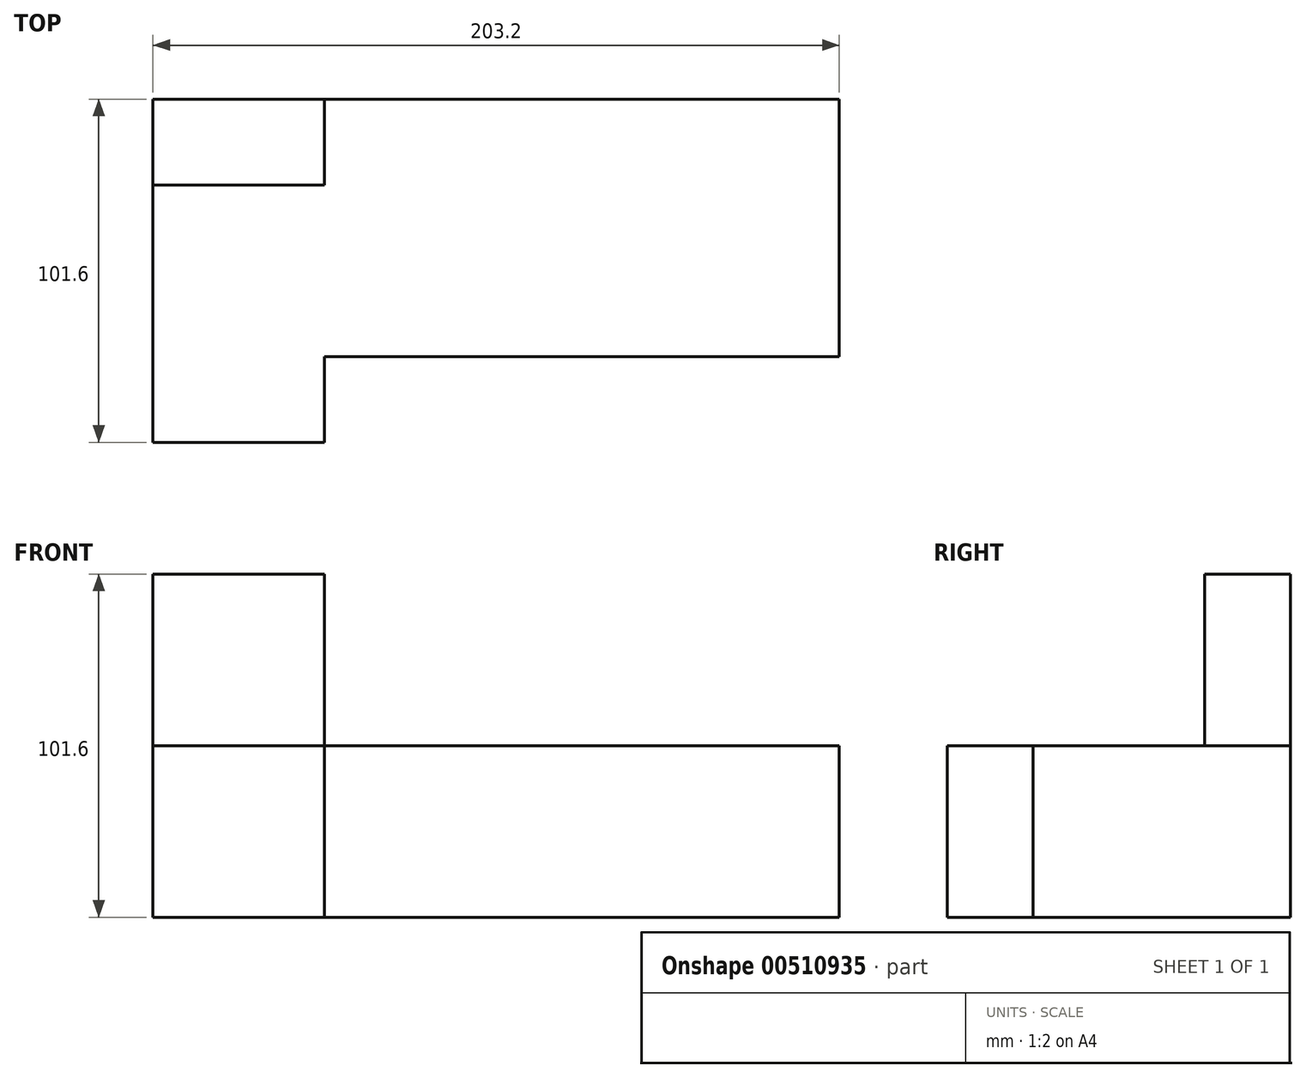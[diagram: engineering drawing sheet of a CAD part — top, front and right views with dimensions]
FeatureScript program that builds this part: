
annotation { "Feature Type Name" : "Feature", "Feature Type Description" : "" }
export const myFeature = defineFeature(function(context is Context, id is Id, definition is map)
    precondition{}
    {
        {
            var Q0;
            Q0=qCreatedBy(makeId("Front.planeOp"),FACE);
            var sketch = newSketch(context, id + "F0", { "sketchPlane" : qUnion([Q0])});
            skLineSegment(sketch, "E0.bottom", {"start": v(-100.78, 50.8) * mm, "end": v(102.42, 50.8) * mm});
            skLineSegment(sketch, "E0.top", {"start": v(-100.78, 0) * mm, "end": v(102.42, 0) * mm});
            skLineSegment(sketch, "E0.left", {"start": v(-100.78, 50.8) * mm, "end": v(-100.78, 0) * mm});
            skLineSegment(sketch, "E0.right", {"start": v(102.42, 50.8) * mm, "end": v(102.42, 0) * mm});
            skSolve(sketch);
        }
        {
            var Q0;
            Q0=makeQuery(id+"F0.imprint","IMPRINT",FACE,{"disambiguationData":[TD([[makeQuery(id+"F0.imprint","IMPRINT",EDGE,{"derivedFrom":sQuery(id+"F0.wireOp",EDGE,"E0.bottom")}),-1.0]])]});
            extrude(context, id + "F1", {"entities" : qUnion([Q0]), "depth" : 76.2 * mm});
        }
        {
            var Q0;
            Q0=makeQuery(id+"F1.opExtrude","CAP_FACE",FACE,{"disambiguationData":[OSD([sQuery(id+"F0.wireOp",EDGE,"E0.bottom"),sQuery(id+"F0.wireOp",EDGE,"E0.top"),sQuery(id+"F0.wireOp",EDGE,"E0.left"),sQuery(id+"F0.wireOp",EDGE,"E0.right")])],"isStart":false});
            var sketch = newSketch(context, id + "F2", { "sketchPlane" : qUnion([Q0])});
            skLineSegment(sketch, "E1.bottom", {"start": v(-100.78, 0) * mm, "end": v(-49.98, 0) * mm});
            skLineSegment(sketch, "E1.top", {"start": v(-100.78, 50.8) * mm, "end": v(-49.98, 50.8) * mm});
            skLineSegment(sketch, "E1.left", {"start": v(-100.78, 0) * mm, "end": v(-100.78, 50.8) * mm});
            skLineSegment(sketch, "E1.right", {"start": v(-49.98, 0) * mm, "end": v(-49.98, 50.8) * mm});
            skSolve(sketch);
        }
        {
            var Q0;
            Q0=makeQuery(id+"F2.imprint","IMPRINT",FACE,{"disambiguationData":[TD([[makeQuery(id+"F2.imprint","IMPRINT",EDGE,{"derivedFrom":sQuery(id+"F2.wireOp",EDGE,"E1.bottom")}),1.0]])]});
            extrude(context, id + "F3", {"entities" : qUnion([Q0]), "operationType" : NewBodyOperationType.ADD, "depth" : 25.4 * mm});
        }
        {
            var Q0;
            Q0=makeQuery(id+"F3.boolean.opBoolean","MERGE",FACE,{"derivedFrom":[makeQuery(id+"F1.opExtrude","SWEPT_FACE",FACE,{"disambiguationData":[OSD([sQuery(id+"F0.wireOp",EDGE,"E0.bottom")])]}),makeQuery(id+"F3.opExtrude","SWEPT_FACE",FACE,{"disambiguationData":[OSD([sQuery(id+"F2.wireOp",EDGE,"E1.top")])]})]});
            var sketch = newSketch(context, id + "F4", { "sketchPlane" : qUnion([Q0])});
            skLineSegment(sketch, "E2.bottom", {"start": v(-100.78, 0) * mm, "end": v(-49.98, 0) * mm});
            skLineSegment(sketch, "E2.top", {"start": v(-100.78, -25.4) * mm, "end": v(-49.98, -25.4) * mm});
            skLineSegment(sketch, "E2.left", {"start": v(-100.78, 0) * mm, "end": v(-100.78, -25.4) * mm});
            skLineSegment(sketch, "E2.right", {"start": v(-49.98, 0) * mm, "end": v(-49.98, -25.4) * mm});
            skSolve(sketch);
        }
        {
            var Q0;
            Q0=makeQuery(id+"F4.imprint","IMPRINT",FACE,{"disambiguationData":[TD([[makeQuery(id+"F4.imprint","IMPRINT",EDGE,{"derivedFrom":sQuery(id+"F4.wireOp",EDGE,"E2.bottom")}),-1.0]])]});
            extrude(context, id + "F5", {"entities" : qUnion([Q0]), "operationType" : NewBodyOperationType.ADD, "depth" : 50.8 * mm});
        }
    });
